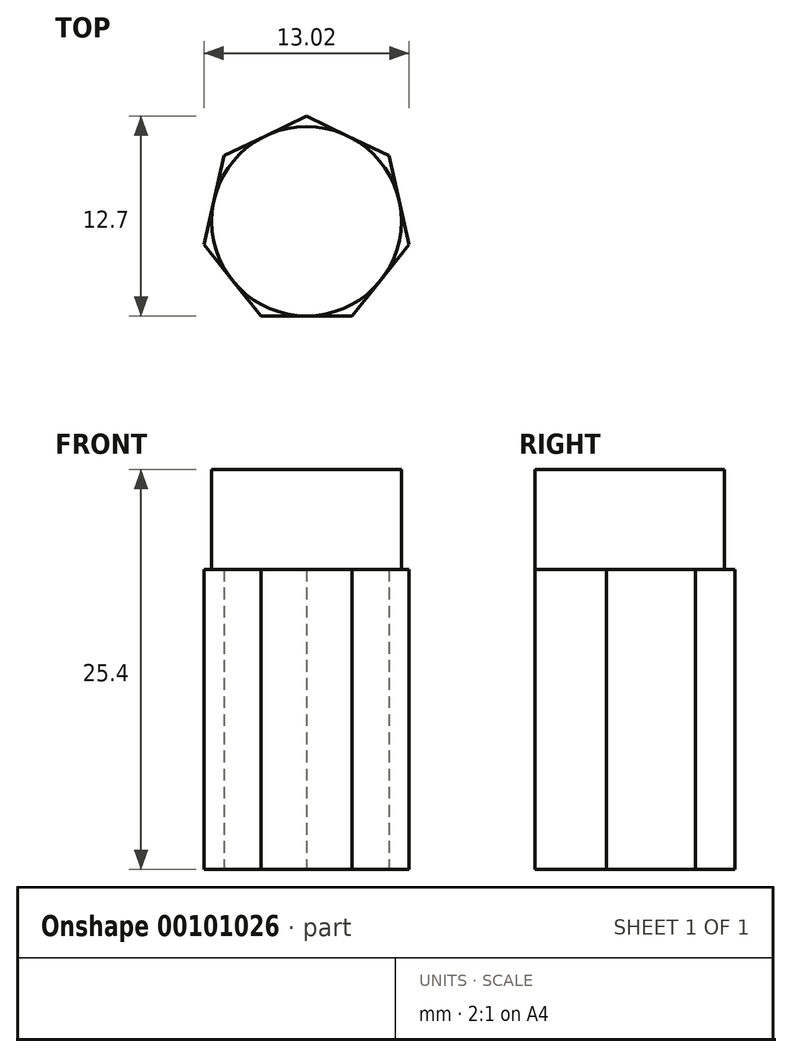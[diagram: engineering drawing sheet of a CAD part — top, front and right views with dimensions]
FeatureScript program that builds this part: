
annotation { "Feature Type Name" : "Feature", "Feature Type Description" : "" }
export const myFeature = defineFeature(function(context is Context, id is Id, definition is map)
    precondition{}
    {
        {
            var Q0;
            Q0=qCreatedBy(makeId("Top.planeOp"),FACE);
            var sketch = newSketch(context, id + "F0", { "sketchPlane" : qUnion([Q0])});
            skCircle(sketch, "E0.cCircle", {"center": v(0, 0) * mm, "radius": 6.02 * mm, "construction": true});
            skLineSegment(sketch, "E0.0", {"start": v(0, 6.68) * mm, "end": v(5.22, 4.17) * mm});
            skLineSegment(sketch, "E0.1", {"start": v(5.22, 4.17) * mm, "end": v(6.51, -1.49) * mm});
            skLineSegment(sketch, "E0.2", {"start": v(6.51, -1.49) * mm, "end": v(2.9, -6.02) * mm});
            skLineSegment(sketch, "E0.3", {"start": v(2.9, -6.02) * mm, "end": v(-2.9, -6.02) * mm});
            skLineSegment(sketch, "E0.4", {"start": v(-2.9, -6.02) * mm, "end": v(-6.51, -1.49) * mm});
            skLineSegment(sketch, "E0.5", {"start": v(-6.51, -1.49) * mm, "end": v(-5.22, 4.17) * mm});
            skLineSegment(sketch, "E0.6", {"start": v(-5.22, 4.17) * mm, "end": v(0, 6.68) * mm});
            skPoint(sketch, "E0.0.midPoint", {"position": v(2.61, 5.42) * mm});
            skCircle(sketch, "E1", {"center": v(0, 0) * mm, "radius": 4.76 * mm});
            skSolve(sketch);
        }
        {
            var Q0;
            Q0=makeQuery(id+"F0.imprint","IMPRINT",FACE,{"disambiguationData":[TD([[makeQuery(id+"F0.imprint","IMPRINT",EDGE,{"derivedFrom":sQuery(id+"F0.wireOp",EDGE,"E0.0")}),-1.0]])]});
            var Q1;
            Q1=makeQuery(id+"F0.imprint","IMPRINT",FACE,{"disambiguationData":[TD([[makeQuery(id+"F0.imprint","IMPRINT",EDGE,{"derivedFrom":sQuery(id+"F0.wireOp",EDGE,"E1")}),1.0]])]});
            extrude(context, id + "F1", {"entities" : qUnion([Q0, Q1]), "depth" : 19.05 * mm});
        }
        {
            var Q0;
            Q0=makeQuery(id+"F1.opExtrude","CAP_FACE",FACE,{"disambiguationData":[OSD([sQuery(id+"F0.wireOp",EDGE,"E0.0"),sQuery(id+"F0.wireOp",EDGE,"E0.1"),sQuery(id+"F0.wireOp",EDGE,"E0.2"),sQuery(id+"F0.wireOp",EDGE,"E0.3"),sQuery(id+"F0.wireOp",EDGE,"E0.4"),sQuery(id+"F0.wireOp",EDGE,"E0.5"),sQuery(id+"F0.wireOp",EDGE,"E0.6")])],"isStart":false});
            var sketch = newSketch(context, id + "F2", { "sketchPlane" : qUnion([Q0])});
            skCircle(sketch, "E2", {"center": v(0, 0) * mm, "radius": 6.02 * mm});
            skSolve(sketch);
        }
        {
            var Q0;
            {var subQ0=sQuery(id+"F2.wireOp",EDGE,"E2");var subQ4=makeQuery(id+"F2.imprint","INTERSECT",VERTEX,{"derivedFrom":[makeQuery(id+"F1.opExtrude","CAP_EDGE",EDGE,{"disambiguationData":[OSD([sQuery(id+"F0.wireOp",EDGE,"E0.0")])],"isStart":false}),subQ0]});Q0=makeQuery(id+"F2.imprint","IMPRINT",FACE,{"disambiguationData":[TD([[makeQuery(id+"F2.imprint","IMPRINT",EDGE,{"disambiguationData":[TD([[subQ4,1.0]])],"derivedFrom":subQ0}),1.0]])]});}
            cPlane(context, id + "F3", {"entities" : qUnion([Q0]), "cplaneType" : CPlaneType.OFFSET, "offset" : 6.35 * mm, "width" : 152.4 * mm, "height" : 152.4 * mm});
        }
        {
            var Q0;
            Q0=qCreatedBy(id+"F3.planeOp",FACE);
            var sketch = newSketch(context, id + "F4", { "sketchPlane" : qUnion([Q0])});
            skCircle(sketch, "E3", {"center": v(0, 0) * mm, "radius": 6.02 * mm});
            skSolve(sketch);
        }
        {
            var Q1;
            {var subQ0=sQuery(id+"F2.wireOp",EDGE,"E2");var subQ4=makeQuery(id+"F2.imprint","INTERSECT",VERTEX,{"derivedFrom":[makeQuery(id+"F1.opExtrude","CAP_EDGE",EDGE,{"disambiguationData":[OSD([sQuery(id+"F0.wireOp",EDGE,"E0.0")])],"isStart":false}),subQ0]});Q1=makeQuery(id+"F2.imprint","IMPRINT",FACE,{"disambiguationData":[TD([[makeQuery(id+"F2.imprint","IMPRINT",EDGE,{"disambiguationData":[TD([[subQ4,1.0]])],"derivedFrom":subQ0}),1.0]])]});}
            var Q2;
            Q2=makeQuery(id+"F4.imprint","IMPRINT",FACE,{"disambiguationData":[TD([[makeQuery(id+"F4.imprint","IMPRINT",EDGE,{"derivedFrom":sQuery(id+"F4.wireOp",EDGE,"E3")}),1.0]])]});
            loft(context, id + "F5", {"operationType" : NewBodyOperationType.ADD, "sheetProfilesArray" : [{ "sheetProfileEntities" : qUnion([Q1]) }, { "sheetProfileEntities" : qUnion([Q2]) }]});
        }
    });
